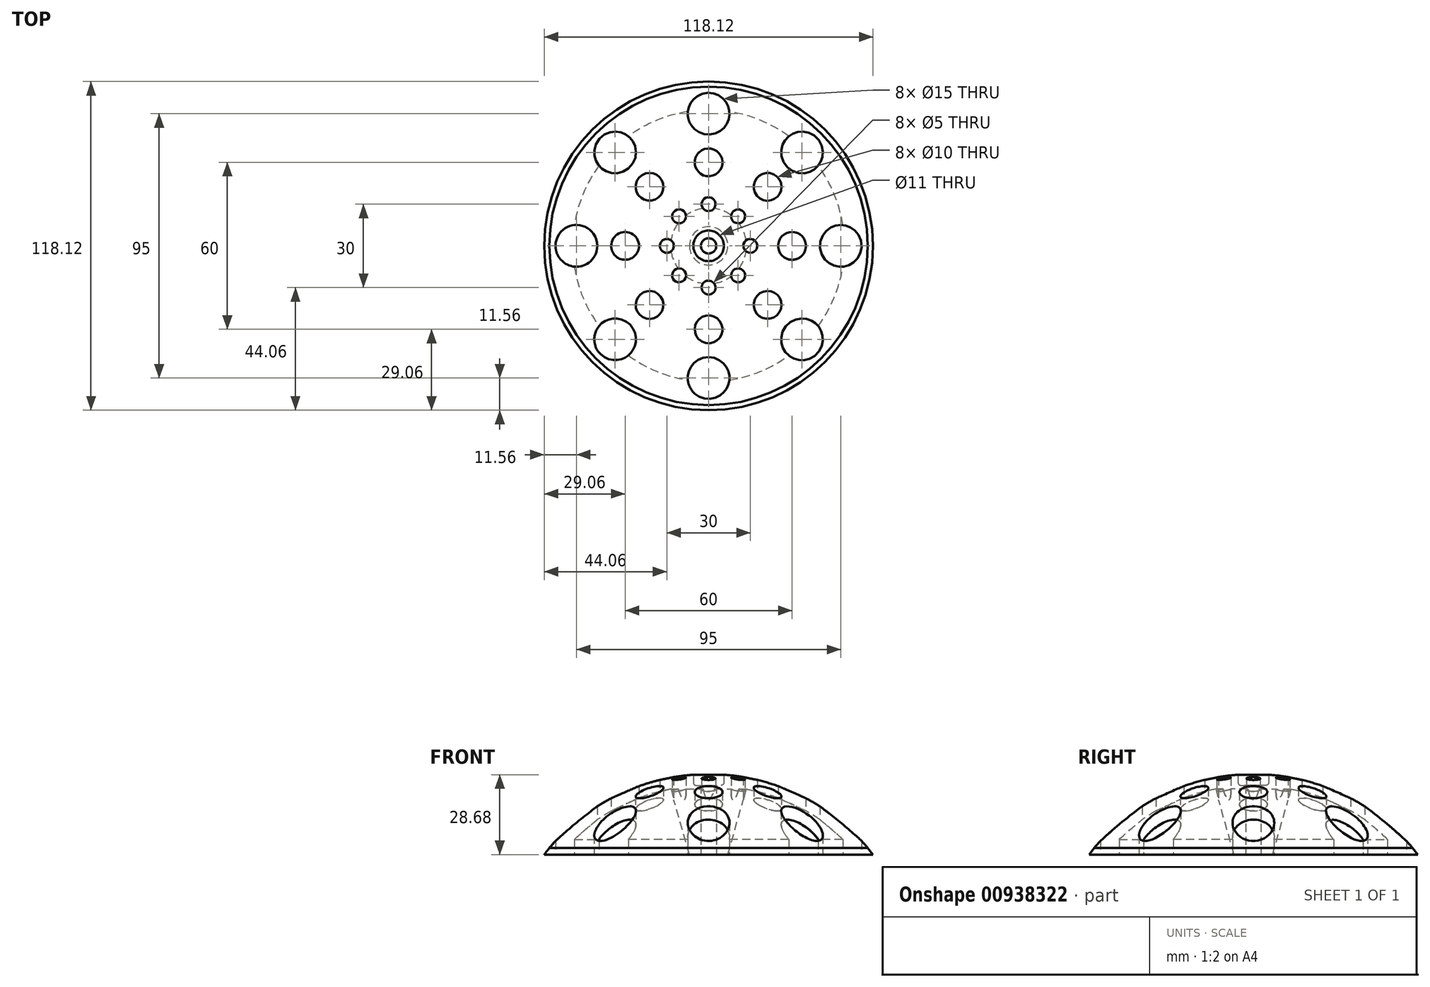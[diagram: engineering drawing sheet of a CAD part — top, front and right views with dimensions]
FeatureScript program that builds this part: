
annotation { "Feature Type Name" : "Feature", "Feature Type Description" : "" }
export const myFeature = defineFeature(function(context is Context, id is Id, definition is map)
    precondition{}
    {
        {
            var Q0;
            Q0=qCreatedBy(makeId("Front.planeOp"),FACE);
            var sketch = newSketch(context, id + "F0", { "sketchPlane" : qUnion([Q0])});
            skArc(sketch, "E0", {"start": v(-5.5, 74.8) * mm, "mid": v(2.83, -74.95) * mm, "end": v(-0.16, 75) * mm});
            skLineSegment(sketch, "E1", {"start": v(-60.91, 43.76) * mm, "end": v(-57.21, 48.5) * mm});
            skLineSegment(sketch, "E2", {"start": v(-59.06, 46.12) * mm, "end": v(59.14, 46.12) * mm});
            skLineSegment(sketch, "E3", {"start": v(0, 65) * mm, "end": v(0, 75) * mm});
            skLineSegment(sketch, "E4", {"start": v(-4.16, 71) * mm, "end": v(-2.75, 71) * mm});
            skLineSegment(sketch, "E5", {"start": v(-2.75, 71) * mm, "end": v(-4.5, 71) * mm});
            skLineSegment(sketch, "E6", {"start": v(-5.5, 72) * mm, "end": v(-5.5, 74.8) * mm});
            skLineSegment(sketch, "E7", {"start": v(-2.75, 71) * mm, "end": v(-2.75, 64.94) * mm});
            skPoint(sketch, "E8.orphan", {"position": v(0, 71) * mm});
            skArc(sketch, "E9", {"start": v(-13.62, 69.68) * mm, "mid": v(-32.5, 63.12) * mm, "end": v(-48.82, 51.56) * mm});
            skArc(sketch, "E10.trimOffspring", {"start": v(-45.8, 46.12) * mm, "mid": v(24.77, -60.1) * mm, "end": v(0, 65) * mm});
            skLineSegment(sketch, "E11", {"start": v(-48.82, 46.12) * mm, "end": v(-48.82, 51.56) * mm});
            skArc(sketch, "E12.trimOffspring", {"start": v(-53.98, 46.12) * mm, "mid": v(29.72, -64.48) * mm, "end": v(0, 71) * mm});
            skLineSegment(sketch, "E13", {"start": v(-2.75, 64.94) * mm, "end": v(-2.75, 0) * mm});
            skLineSegment(sketch, "E14", {"start": v(-13.62, 69.68) * mm, "end": v(-6.9, 46.12) * mm});
            skPoint(sketch, "E15.visualSharp", {"position": v(-5.5, 71) * mm});
            skArc(sketch, "E15.filletArc", {"start": v(-5.5, 72) * mm, "mid": v(-5.2, 71.3) * mm, "end": v(-4.5, 71) * mm});
            skSolve(sketch);
        }
        {
            var Q0;
            {var subQ5=sQuery(id+"F0.wireOp",EDGE,"E6");Q0=makeQuery(id+"F0.imprint","IMPRINT",FACE,{"disambiguationData":[TD([[makeQuery(id+"F0.imprint","IMPRINT",EDGE,{"derivedFrom":subQ5}),1.0]])]});}
            var Q1;
            Q1=sQuery(id+"F0.wireOp",EDGE,"E3");
            revolve(context, id + "F1", {"surfaceOperationType" : NewSurfaceOperationType.NEW, "entities" : qUnion([Q0]), "axis" : qUnion([Q1]), "revolveType" : RevolveType.FULL});
        }
        {
            var Q0;
            Q0=qCreatedBy(makeId("Top.planeOp"),FACE);
            var sketch = newSketch(context, id + "F2", { "sketchPlane" : qUnion([Q0])});
            skCircle(sketch, "E16", {"center": v(0, 0) * mm, "radius": 60 * mm});
            skCircle(sketch, "E17", {"center": v(0, 30) * mm, "radius": 5 * mm});
            skCircle(sketch, "E18", {"center": v(0, 47.5) * mm, "radius": 7.5 * mm});
            skCircle(sketch, "E19", {"center": v(0, 15) * mm, "radius": 2.5 * mm});
            skCircle(sketch, "E20.1.0", {"center": v(-33.59, 33.59) * mm, "radius": 7.5 * mm});
            skCircle(sketch, "E20.1.1", {"center": v(-21.21, 21.21) * mm, "radius": 5 * mm});
            skCircle(sketch, "E20.1.2", {"center": v(-10.6, 10.6) * mm, "radius": 2.5 * mm});
            skCircle(sketch, "E20.2.0", {"center": v(-47.5, 0) * mm, "radius": 7.5 * mm});
            skCircle(sketch, "E20.2.1", {"center": v(-30, 0) * mm, "radius": 5 * mm});
            skCircle(sketch, "E20.2.2", {"center": v(-15, 0) * mm, "radius": 2.5 * mm});
            skCircle(sketch, "E20.3.0", {"center": v(-33.59, -33.59) * mm, "radius": 7.5 * mm});
            skCircle(sketch, "E20.3.1", {"center": v(-21.21, -21.21) * mm, "radius": 5 * mm});
            skCircle(sketch, "E20.3.2", {"center": v(-10.6, -10.6) * mm, "radius": 2.5 * mm});
            skCircle(sketch, "E20.4.0", {"center": v(0, -47.5) * mm, "radius": 7.5 * mm});
            skCircle(sketch, "E20.4.1", {"center": v(0, -30) * mm, "radius": 5 * mm});
            skCircle(sketch, "E20.4.2", {"center": v(0, -15) * mm, "radius": 2.5 * mm});
            skCircle(sketch, "E20.5.0", {"center": v(33.59, -33.59) * mm, "radius": 7.5 * mm});
            skCircle(sketch, "E20.5.1", {"center": v(21.21, -21.21) * mm, "radius": 5 * mm});
            skCircle(sketch, "E20.5.2", {"center": v(10.6, -10.6) * mm, "radius": 2.5 * mm});
            skCircle(sketch, "E20.6.0", {"center": v(47.5, 0) * mm, "radius": 7.5 * mm});
            skCircle(sketch, "E20.6.1", {"center": v(30, 0) * mm, "radius": 5 * mm});
            skCircle(sketch, "E20.6.2", {"center": v(15, 0) * mm, "radius": 2.5 * mm});
            skCircle(sketch, "E20.7.0", {"center": v(33.59, 33.59) * mm, "radius": 7.5 * mm});
            skCircle(sketch, "E20.7.1", {"center": v(21.21, 21.21) * mm, "radius": 5 * mm});
            skCircle(sketch, "E20.7.2", {"center": v(10.6, 10.6) * mm, "radius": 2.5 * mm});
            skSolve(sketch);
        }
        {
            var Q0;
            Q0=makeQuery(id+"F2.imprint","IMPRINT",FACE,{"disambiguationData":[TD([[makeQuery(id+"F2.imprint","IMPRINT",EDGE,{"derivedFrom":sQuery(id+"F2.wireOp",EDGE,"E20.3.0")}),1.0]])]});
            var Q1;
            Q1=makeQuery(id+"F2.imprint","IMPRINT",FACE,{"disambiguationData":[TD([[makeQuery(id+"F2.imprint","IMPRINT",EDGE,{"derivedFrom":sQuery(id+"F2.wireOp",EDGE,"E20.1.0")}),1.0]])]});
            var Q2;
            Q2=makeQuery(id+"F2.imprint","IMPRINT",FACE,{"disambiguationData":[TD([[makeQuery(id+"F2.imprint","IMPRINT",EDGE,{"derivedFrom":sQuery(id+"F2.wireOp",EDGE,"E20.2.0")}),1.0]])]});
            var Q3;
            Q3=makeQuery(id+"F2.imprint","IMPRINT",FACE,{"disambiguationData":[TD([[makeQuery(id+"F2.imprint","IMPRINT",EDGE,{"derivedFrom":sQuery(id+"F2.wireOp",EDGE,"E18")}),1.0]])]});
            var Q4;
            Q4=makeQuery(id+"F2.imprint","IMPRINT",FACE,{"disambiguationData":[TD([[makeQuery(id+"F2.imprint","IMPRINT",EDGE,{"derivedFrom":sQuery(id+"F2.wireOp",EDGE,"E17")}),1.0]])]});
            var Q5;
            Q5=makeQuery(id+"F2.imprint","IMPRINT",FACE,{"disambiguationData":[TD([[makeQuery(id+"F2.imprint","IMPRINT",EDGE,{"derivedFrom":sQuery(id+"F2.wireOp",EDGE,"E20.1.1")}),1.0]])]});
            var Q6;
            Q6=makeQuery(id+"F2.imprint","IMPRINT",FACE,{"disambiguationData":[TD([[makeQuery(id+"F2.imprint","IMPRINT",EDGE,{"derivedFrom":sQuery(id+"F2.wireOp",EDGE,"E20.2.1")}),1.0]])]});
            var Q7;
            Q7=makeQuery(id+"F2.imprint","IMPRINT",FACE,{"disambiguationData":[TD([[makeQuery(id+"F2.imprint","IMPRINT",EDGE,{"derivedFrom":sQuery(id+"F2.wireOp",EDGE,"E20.7.1")}),1.0]])]});
            var Q8;
            Q8=makeQuery(id+"F2.imprint","IMPRINT",FACE,{"disambiguationData":[TD([[makeQuery(id+"F2.imprint","IMPRINT",EDGE,{"derivedFrom":sQuery(id+"F2.wireOp",EDGE,"E20.7.0")}),1.0]])]});
            var Q9;
            Q9=makeQuery(id+"F2.imprint","IMPRINT",FACE,{"disambiguationData":[TD([[makeQuery(id+"F2.imprint","IMPRINT",EDGE,{"derivedFrom":sQuery(id+"F2.wireOp",EDGE,"E20.6.1")}),1.0]])]});
            var Q10;
            Q10=makeQuery(id+"F2.imprint","IMPRINT",FACE,{"disambiguationData":[TD([[makeQuery(id+"F2.imprint","IMPRINT",EDGE,{"derivedFrom":sQuery(id+"F2.wireOp",EDGE,"E20.6.0")}),1.0]])]});
            var Q11;
            Q11=makeQuery(id+"F2.imprint","IMPRINT",FACE,{"disambiguationData":[TD([[makeQuery(id+"F2.imprint","IMPRINT",EDGE,{"derivedFrom":sQuery(id+"F2.wireOp",EDGE,"E20.5.0")}),1.0]])]});
            var Q12;
            Q12=makeQuery(id+"F2.imprint","IMPRINT",FACE,{"disambiguationData":[TD([[makeQuery(id+"F2.imprint","IMPRINT",EDGE,{"derivedFrom":sQuery(id+"F2.wireOp",EDGE,"E20.5.1")}),1.0]])]});
            var Q13;
            Q13=makeQuery(id+"F2.imprint","IMPRINT",FACE,{"disambiguationData":[TD([[makeQuery(id+"F2.imprint","IMPRINT",EDGE,{"derivedFrom":sQuery(id+"F2.wireOp",EDGE,"E20.4.0")}),1.0]])]});
            var Q14;
            Q14=makeQuery(id+"F2.imprint","IMPRINT",FACE,{"disambiguationData":[TD([[makeQuery(id+"F2.imprint","IMPRINT",EDGE,{"derivedFrom":sQuery(id+"F2.wireOp",EDGE,"E20.4.1")}),1.0]])]});
            var Q15;
            Q15=makeQuery(id+"F2.imprint","IMPRINT",FACE,{"disambiguationData":[TD([[makeQuery(id+"F2.imprint","IMPRINT",EDGE,{"derivedFrom":sQuery(id+"F2.wireOp",EDGE,"E20.3.1")}),1.0]])]});
            var Q16;
            Q16=makeQuery(id+"F2.imprint","IMPRINT",FACE,{"disambiguationData":[TD([[makeQuery(id+"F2.imprint","IMPRINT",EDGE,{"derivedFrom":sQuery(id+"F2.wireOp",EDGE,"E20.3.2")}),1.0]])]});
            var Q17;
            Q17=makeQuery(id+"F2.imprint","IMPRINT",FACE,{"disambiguationData":[TD([[makeQuery(id+"F2.imprint","IMPRINT",EDGE,{"derivedFrom":sQuery(id+"F2.wireOp",EDGE,"E20.2.2")}),1.0]])]});
            var Q18;
            Q18=makeQuery(id+"F2.imprint","IMPRINT",FACE,{"disambiguationData":[TD([[makeQuery(id+"F2.imprint","IMPRINT",EDGE,{"derivedFrom":sQuery(id+"F2.wireOp",EDGE,"E20.1.2")}),1.0]])]});
            var Q19;
            Q19=makeQuery(id+"F2.imprint","IMPRINT",FACE,{"disambiguationData":[TD([[makeQuery(id+"F2.imprint","IMPRINT",EDGE,{"derivedFrom":sQuery(id+"F2.wireOp",EDGE,"E19")}),1.0]])]});
            var Q20;
            Q20=makeQuery(id+"F2.imprint","IMPRINT",FACE,{"disambiguationData":[TD([[makeQuery(id+"F2.imprint","IMPRINT",EDGE,{"derivedFrom":sQuery(id+"F2.wireOp",EDGE,"E20.7.2")}),1.0]])]});
            var Q21;
            Q21=makeQuery(id+"F2.imprint","IMPRINT",FACE,{"disambiguationData":[TD([[makeQuery(id+"F2.imprint","IMPRINT",EDGE,{"derivedFrom":sQuery(id+"F2.wireOp",EDGE,"E20.6.2")}),1.0]])]});
            var Q22;
            Q22=makeQuery(id+"F2.imprint","IMPRINT",FACE,{"disambiguationData":[TD([[makeQuery(id+"F2.imprint","IMPRINT",EDGE,{"derivedFrom":sQuery(id+"F2.wireOp",EDGE,"E20.5.2")}),1.0]])]});
            var Q23;
            Q23=makeQuery(id+"F2.imprint","IMPRINT",FACE,{"disambiguationData":[TD([[makeQuery(id+"F2.imprint","IMPRINT",EDGE,{"derivedFrom":sQuery(id+"F2.wireOp",EDGE,"E20.4.2")}),1.0]])]});
            extrude(context, id + "F3", {"entities" : qUnion([Q0, Q1, Q2, Q3, Q4, Q5, Q6, Q7, Q8, Q9, Q10, Q11, Q12, Q13, Q14, Q15, Q16, Q17, Q18, Q19, Q20, Q21, Q22, Q23]), "operationType" : NewBodyOperationType.REMOVE, "depth" : 100 * mm, "offsetDistance" : 25 * mm});
        }
    });
